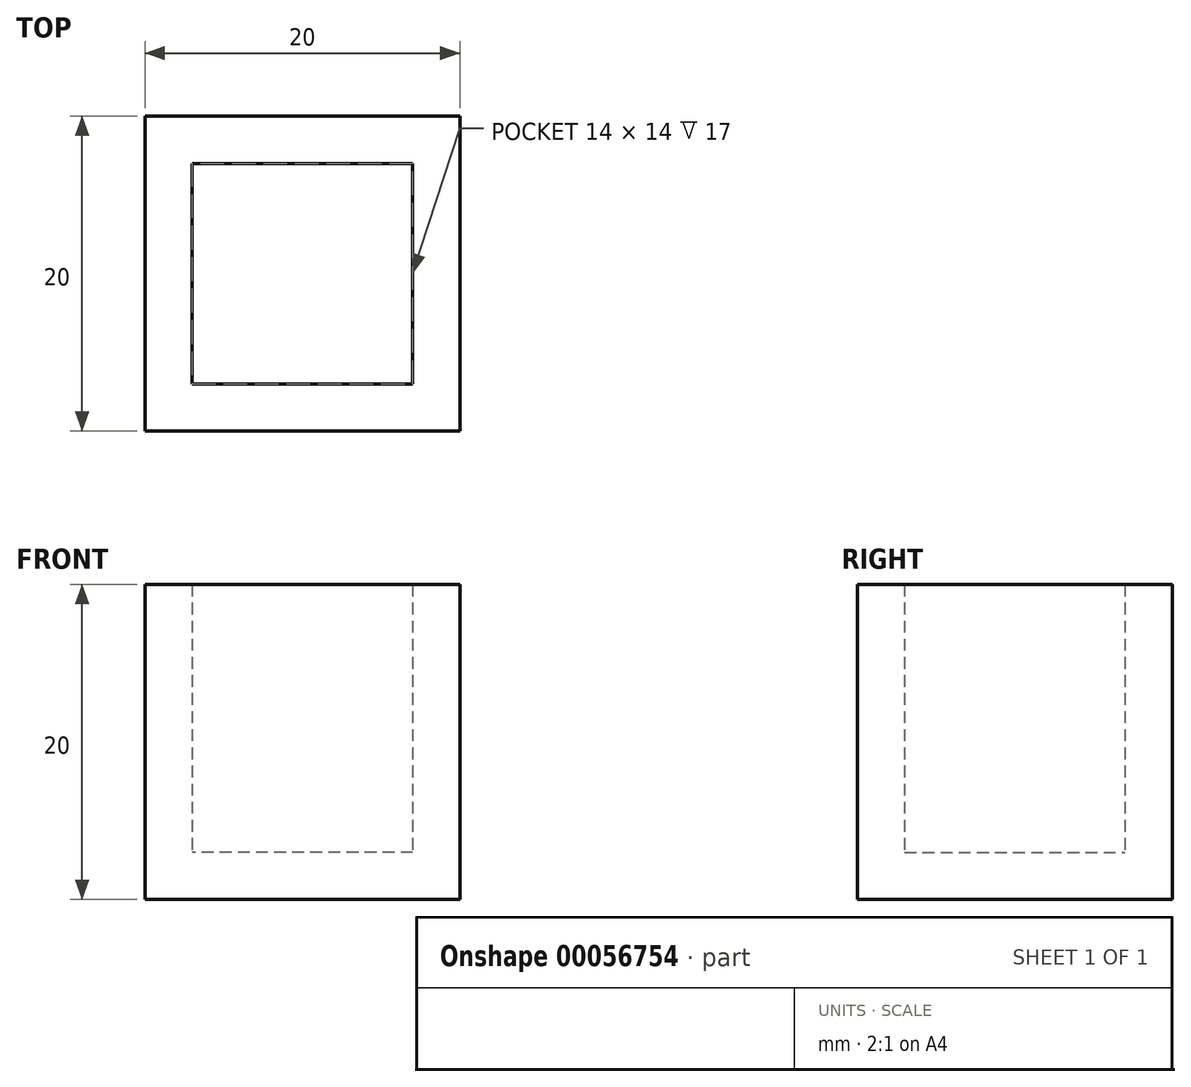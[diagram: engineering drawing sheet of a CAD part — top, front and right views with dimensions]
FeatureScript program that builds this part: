
annotation { "Feature Type Name" : "Feature", "Feature Type Description" : "" }
export const myFeature = defineFeature(function(context is Context, id is Id, definition is map)
    precondition{}
    {
        {
            var Q0;
            Q0=qCreatedBy(makeId("Top.planeOp"),FACE);
            var sketch = newSketch(context, id + "F0", { "sketchPlane" : qUnion([Q0])});
            skLineSegment(sketch, "E0.rect.bottom", {"start": v(10, -10) * mm, "end": v(-10, -10) * mm});
            skLineSegment(sketch, "E0.rect.top", {"start": v(10, 10) * mm, "end": v(-10, 10) * mm});
            skLineSegment(sketch, "E0.rect.left", {"start": v(10, -10) * mm, "end": v(10, 10) * mm});
            skLineSegment(sketch, "E0.rect.right", {"start": v(-10, -10) * mm, "end": v(-10, 10) * mm});
            skPoint(sketch, "E0.rect.middle", {"position": v(0, 0) * mm});
            skSolve(sketch);
        }
        {
            var Q0;
            Q0 = qSketchRegion(id + "F0", true);
            extrude(context, id + "F1", {"entities" : qUnion([Q0]), "depth" : 20 * mm});
        }
        {
            var Q0;
            Q0=makeQuery(id+"F1.opExtrude","CAP_FACE",FACE,{"disambiguationData":[OSD([sQuery(id+"F0.wireOp",EDGE,"E0.rect.bottom"),sQuery(id+"F0.wireOp",EDGE,"E0.rect.top"),sQuery(id+"F0.wireOp",EDGE,"E0.rect.left"),sQuery(id+"F0.wireOp",EDGE,"E0.rect.right")])],"isStart":false});
            shell(context, id + "F2", {"entities" : qUnion([Q0]), "thickness" : 3 * mm});
        }
    });
